FCSTD DOCUMENT  (FreeCAD 0.19R)
Label: tool_support
License: All rights reserved
LicenseURL: http://en.wikipedia.org/wiki/All_rights_reserved
objects: App::DocumentObjectGroup×2, App::Link×2, PartDesign::CoordinateSystem×1, App::FeaturePython×1, App::Part×1
note: 1 computed .brp shape members not serialized (recipe doc carries the construction recipe); baked Part::Feature solids carry a one-line shape summary decoded from their .brp
EXTERNAL_REF file=platform.FCStd obj=LCS_1
EXTERNAL_REF file=platform.FCStd obj=Body
EXTERNAL_REF file=lower_support.FCStd obj=LCS_hole1
EXTERNAL_REF file=platform.FCStd obj=LCS_hole1
EXTERNAL_REF file=lower_support.FCStd obj=Body

FEATURE [App::DocumentObjectGroup] Parts
FEATURE [PartDesign::CoordinateSystem] LCS_Origin
  AttacherType = Attacher::AttachEngine3D
  MapMode = 2
  Support = -> [X_Axis]
FEATURE [App::DocumentObjectGroup] Constraints
FEATURE [App::FeaturePython] Variables  # WARN: FeaturePython — macro-defined, semantics opaque (R4)
FEATURE [App::Link] Unnamed1_platform
  AssemblyType = Asm4EE
  AttachedBy = #LCS_1
  AttachedTo = Parent Assembly#LCS_Origin
  LinkPlacement = pos=(3e-16,-8e-16,-10) rot=(0,0,1;0rad)
  LinkedObject = -> <external platform.FCStd>#Body
  Placement = pos=(3e-16,-8e-16,-10) rot=(0,0,1;0rad)
  expr: Placement = LCS_Origin.Placement * AttachmentOffset * platform#LCS_1.Placement ^ -1
FEATURE [App::Link] lower_support_Body
  AssemblyType = Asm4EE
  AttachedBy = #LCS_hole1
  AttachedTo = Unnamed1_platform#LCS_hole1
  AttachmentOffset = pos=(0,0,0) rot=(1,0,0;3.14159rad)
  LinkPlacement = pos=(1.95e-14,100,2.03e-14) rot=(0,0,1;0rad)
  LinkedObject = -> <external lower_support.FCStd>#Body
  Placement = pos=(1.95e-14,100,2.03e-14) rot=(0,0,1;0rad)
  expr: Placement = Unnamed1_platform.Placement * platform#LCS_hole1.Placement * AttachmentOffset * lower_support#LCS_hole1.Placement ^ -1
FEATURE [App::Part] Model
  Configuration = 0
  Group = -> [LCS_Origin,Constraints,Variables,Unnamed1_platform,lower_support_Body]
  Origin = -> Origin
  Type = Assembly4 Model

RESOLVED EXTERNAL PARTS (link-assembly join: the EXTERNAL_REF files above that resolve inside this repo's crawl, each included once):
---- part lower_support.FCStd = doc fcstd_1ed02091a3f0 ----
FCSTD DOCUMENT  (FreeCAD 0.19R)
Label: lower_support
License: All rights reserved
LicenseURL: http://en.wikipedia.org/wiki/All_rights_reserved
objects: Sketcher::SketchObject×5, PartDesign::CoordinateSystem×5, PartDesign::Pad×3, PartDesign::Point×3, PartDesign::Hole×2, PartDesign::Plane×1, PartDesign::Body×1
note: 25 computed .brp shape members not serialized (recipe doc carries the construction recipe); baked Part::Feature solids carry a one-line shape summary decoded from their .brp

FEATURE [Sketcher::SketchObject] Sketch
  FullyConstrained = true
  MapMode = 5
  Placement = pos=(0,0,0) rot=(1,0,0;1.5708rad)
  Support = -> [XZ_Plane]
  sketch-geometry (8):
    g0: LineSegment StartX=-32 StartY=32 StartZ=0 EndX=32 EndY=32 EndZ=0
    g1: LineSegment StartX=-28 StartY=28 StartZ=0 EndX=-4 EndY=28 EndZ=0
    g2: LineSegment StartX=-4 StartY=4 StartZ=0 EndX=-4 EndY=28 EndZ=0
    g3: LineSegment StartX=4 StartY=28 StartZ=0 EndX=4 EndY=4 EndZ=0
    g4: LineSegment StartX=4 StartY=28 StartZ=0 EndX=28 EndY=28 EndZ=0
    g5: ArcOfCircle CenterX=-28 CenterY=32 CenterZ=0 NormalX=0 NormalY=0 NormalZ=1 AngleXU=0 Radius=4 StartAngle=3.14159 EndAngle=4.71239
    g6: ArcOfCircle CenterX=28 CenterY=32 CenterZ=0 NormalX=0 NormalY=0 NormalZ=1 AngleXU=0 Radius=4 StartAngle=4.71239 EndAngle=6.28319
    g7: ArcOfCircle CenterX=1e-16 CenterY=4 CenterZ=0 NormalX=0 NormalY=0 NormalZ=1 AngleXU=0 Radius=4 StartAngle=3.14159 EndAngle=6.28319
  constraints (25):
    c: Horizontal(g1)
    c: Coincident(g2,g1)
    c: Vertical(g2)
    c: Vertical(g3)
    c: Coincident(g4,g3)
    c: Horizontal(g4)
    c: DistanceX(g2,g3) = 8
    c: DistanceY(g4,g0) = 4
    c: DistanceX(g0,g0) = 64
    c: Symmetric(g1,g3,g-2)
    c: DistanceY(g3,g3) = 24
    c: DistanceY(g2,g1) = 24
    c: DistanceX(g3,g4) = 24
    c: DistanceX(g1,g1) = 24
    c: DistanceY(g-1,g2) = 4
    c: Symmetric(g0,g0,g-2)
    c: Coincident(g5,g0)
    c: PointOnObject(g5,g0)
    c: Coincident(g5,g1)
    c: PointOnObject(g6,g0)
    c: Coincident(g6,g4)
    c: Coincident(g6,g0)
    c: Coincident(g7,g3)
    c: Coincident(g7,g2)
    c: PointOnObject(g-1,g7)
FEATURE [PartDesign::Pad] Pad
  Direction = (1,1,1)
  Length = 200
  Length2 = 100
  Placement = pos=(0,0,0) rot=(1,0,0;1.5708rad)
  Profile = -> Sketch
  Type = 0
FEATURE [PartDesign::CoordinateSystem] LCS_1
  AttacherType = Attacher::AttachEngine3D
  MapMode = 45
  Placement = pos=(0,-200,32) rot=(0.57735,0.57735,0.57735;2.0944rad)
  Support = -> [Pad]
FEATURE [PartDesign::CoordinateSystem] LCS_2
  AttacherType = Attacher::AttachEngine3D
  MapMode = 45
  Placement = pos=(0,0,32) rot=(0.57735,0.57735,0.57735;2.0944rad)
  Support = -> [Pad]
FEATURE [PartDesign::Plane] DatumPlane
  AttachmentOffset = pos=(0,0,0) rot=(0,1,0;1.5708rad)
  Length = 288.534
  MapMode = 5
  Placement = pos=(0,0,0) rot=(-0.57735,0.57735,-0.57735;2.0944rad)
  ResizeMode = 0
  Support = -> [Pad]
  Width = 81.5341
FEATURE [Sketcher::SketchObject] Sketch001
  ExternalGeometry = -> [Pad]
  FullyConstrained = true
  MapMode = 5
  Placement = pos=(0,0,0) rot=(0.57735,-0.57735,0.57735;4.18879rad)
  Support = -> [DatumPlane]
  sketch-geometry (6):
    g0: LineSegment StartX=200 StartY=0 StartZ=0 EndX=232 EndY=-1e-15 EndZ=0
    g1: LineSegment StartX=200 StartY=0 StartZ=0 EndX=200 EndY=-32 EndZ=0
    g2: LineSegment StartX=228 StartY=-4 StartZ=0 EndX=204 EndY=-4 EndZ=0
    g3: LineSegment StartX=204 StartY=-4 StartZ=0 EndX=204 EndY=-28 EndZ=0
    g4: ArcOfCircle CenterX=228 CenterY=0 CenterZ=0 NormalX=0 NormalY=0 NormalZ=1 AngleXU=0 Radius=4 StartAngle=4.71239 EndAngle=6.28319
    g5: ArcOfCircle CenterX=200 CenterY=-28 CenterZ=0 NormalX=0 NormalY=0 NormalZ=1 AngleXU=0 Radius=4 StartAngle=4.71239 EndAngle=6.28319
  constraints (19):
    c: Coincident(g0,g-3)
    c: PointOnObject(g0,g-1)
    c: Coincident(g1,g0)
    c: Vertical(g1)
    c: Horizontal(g2)
    c: Coincident(g3,g2)
    c: Vertical(g3)
    c: DistanceX(g1,g3) = 4
    c: DistanceY(g2,g0) = 4
    c: DistanceX(g0,g0) = 32
    c: DistanceX(g2,g2) = 24
    c: DistanceY(g1,g0) = 32
    c: DistanceY(g3,g2) = 24
    c: PointOnObject(g4,g0)
    c: Coincident(g4,g2)
    c: Coincident(g4,g0)
    c: PointOnObject(g5,g1)
    c: Coincident(g5,g1)
    c: Coincident(g5,g3)
FEATURE [PartDesign::Pad] Pad001
  BaseFeature = -> Pad
  Direction = (1,1,1)
  Length = 20
  Length2 = 100
  Midplane = true
  Placement = pos=(0,0,0) rot=(1,0,0;1.5708rad)
  Profile = -> Sketch001
  Type = 0
FEATURE [Sketcher::SketchObject] Sketch002
  ExternalGeometry = -> [Pad001]
  FullyConstrained = true
  MapMode = 5
  Placement = pos=(0,0,0) rot=(0.57735,-0.57735,0.57735;4.18879rad)
  Support = -> [DatumPlane]
  expr: Constraints[9] = 32
  sketch-geometry (6):
    g0: LineSegment StartX=0 StartY=0 StartZ=0 EndX=-32 EndY=5e-16 EndZ=0
    g1: LineSegment StartX=0 StartY=0 StartZ=0 EndX=0 EndY=-32 EndZ=0
    g2: LineSegment StartX=-28 StartY=-4 StartZ=0 EndX=-4 EndY=-4 EndZ=0
    g3: LineSegment StartX=-4 StartY=-4 StartZ=0 EndX=-4 EndY=-28 EndZ=0
    g4: ArcOfCircle CenterX=-28 CenterY=0 CenterZ=0 NormalX=0 NormalY=0 NormalZ=1 AngleXU=0 Radius=4 StartAngle=3.14159 EndAngle=4.71239
    g5: ArcOfCircle CenterX=0 CenterY=-28 CenterZ=0 NormalX=0 NormalY=0 NormalZ=1 AngleXU=0 Radius=4 StartAngle=3.14159 EndAngle=4.71239
  constraints (19):
    c: Coincident(g0,g-1)
    c: PointOnObject(g0,g-1)
    c: Coincident(g1,g0)
    c: PointOnObject(g1,g-2)
    c: Horizontal(g2)
    c: Coincident(g3,g2)
    c: Vertical(g3)
    c: DistanceY(g3,g2) = 24
    c: DistanceX(g2,g2) = 24
    c: DistanceY(g1,g0) = 32
    c: DistanceX(g0,g0) = 32
    c: DistanceX(g3,g1) = 4
    c: DistanceY(g2,g0) = 4
    c: PointOnObject(g4,g0)
    c: Coincident(g4,g2)
    c: Coincident(g4,g0)
    c: PointOnObject(g5,g1)
    c: Coincident(g5,g1)
    c: Coincident(g5,g3)
FEATURE [PartDesign::Pad] Pad002
  BaseFeature = -> Pad001
  Direction = (1,1,1)
  Length = 100
  Length2 = 100
  Midplane = true
  Placement = pos=(0,0,0) rot=(1,0,0;1.5708rad)
  Profile = -> Sketch002
  Type = 0
FEATURE [Sketcher::SketchObject] Sketch003
  ExternalGeometry = -> [Pad002]
  FullyConstrained = true
  MapMode = 5
  Placement = pos=(0,0,-6.4e-15) rot=(1,0,0;3.14159rad)
  Support = -> [Pad002]
  sketch-geometry (1):
    g0: Circle CenterX=0 CenterY=216 CenterZ=0 NormalX=0 NormalY=0 NormalZ=1 AngleXU=0 Radius=3.25
  constraints (3):
    c: DistanceY(g0,g-3) = 16
    c: PointOnObject(g0,g-2)
    c: Diameter(g0) = 6.5
FEATURE [PartDesign::Hole] Hole
  BaseFeature = -> Pad002
  Depth = 25
  DepthType = 0
  Diameter = 6
  DrillForDepth = false
  DrillPoint = 1
  DrillPointAngle = 118
  HoleCutCountersinkAngle = 90
  HoleCutCustomValues = false
  HoleCutDepth = 0
  HoleCutDiameter = 6.1
  HoleCutType = 0
  ModelActualThread = false
  Placement = pos=(0,0,0) rot=(1,0,0;1.5708rad)
  Profile = -> Sketch003
  Tapered = false
  TaperedAngle = 90
  ThreadAngle = 0
  ThreadClass = 0
  ThreadCutOffInner = 0
  ThreadCutOffOuter = 0
  ThreadDirection = 0
  ThreadFit = 0
  ThreadPitch = 0
  ThreadSize = 0
  ThreadType = 0
  Threaded = false
FEATURE [Sketcher::SketchObject] Sketch004
  ExternalGeometry = -> [Hole]
  FullyConstrained = true
  MapMode = 5
  Placement = pos=(0,0,0) rot=(1,0,0;3.14159rad)
  Support = -> [Hole]
  sketch-geometry (2):
    g0: Circle CenterX=34 CenterY=-16 CenterZ=0 NormalX=0 NormalY=0 NormalZ=1 AngleXU=0 Radius=3.25
    g1: Circle CenterX=-34 CenterY=-16 CenterZ=0 NormalX=0 NormalY=0 NormalZ=1 AngleXU=0 Radius=3.25
  constraints (5):
    c: Equal(g0,g1)
    c: Diameter(g1) = 6.5
    c: Symmetric(g1,g0,g-2)
    c: DistanceX(g-4,g1) = 16
    c: DistanceY(g-4,g1) = 16
FEATURE [PartDesign::Hole] Hole001
  BaseFeature = -> Hole
  Depth = 25
  DepthType = 0
  Diameter = 6
  DrillForDepth = false
  DrillPoint = 1
  DrillPointAngle = 118
  HoleCutCountersinkAngle = 90
  HoleCutCustomValues = false
  HoleCutDepth = 0
  HoleCutDiameter = 6.1
  HoleCutType = 0
  ModelActualThread = false
  Placement = pos=(0,0,0) rot=(1,0,0;1.5708rad)
  Profile = -> Sketch004
  Tapered = false
  TaperedAngle = 90
  ThreadAngle = 0
  ThreadClass = 0
  ThreadCutOffInner = 0
  ThreadCutOffOuter = 0
  ThreadDirection = 0
  ThreadFit = 0
  ThreadPitch = 0
  ThreadSize = 0
  ThreadType = 0
  Threaded = false
FEATURE [PartDesign::CoordinateSystem] LCS_hole2
  AttacherType = Attacher::AttachEngine3D
  MapMode = 11
  Placement = pos=(34,16,-2.9e-14) rot=(0.707107,0.707107,0;3.14159rad)
  Support = -> [Hole001]
FEATURE [PartDesign::CoordinateSystem] LCS_hole3
  AttacherType = Attacher::AttachEngine3D
  MapMode = 11
  Placement = pos=(-34,16,-2.9e-14) rot=(0.707107,0.707107,0;3.14159rad)
  Support = -> [Hole001]
FEATURE [PartDesign::CoordinateSystem] LCS_hole1
  AttacherType = Attacher::AttachEngine3D
  MapMode = 11
  Placement = pos=(0,-216,3.84e-13) rot=(0.707107,0.707107,0;3.14159rad)
  Support = -> [Hole001]
FEATURE [PartDesign::Point] DatumPoint
  AttacherType = Attacher::AttachEnginePoint
  MapMode = 36
  Placement = pos=(34,16,-2.9e-14) rot=(0,-0.707107,0.707107;3.14159rad)
  Support = -> [Hole001]
FEATURE [PartDesign::Point] DatumPoint001
  AttacherType = Attacher::AttachEnginePoint
  MapMode = 36
  Placement = pos=(-34,16,-2.9e-14) rot=(0,-0.707107,0.707107;3.14159rad)
  Support = -> [Hole001]
FEATURE [PartDesign::Point] DatumPoint002
  AttacherType = Attacher::AttachEnginePoint
  MapMode = 36
  Placement = pos=(0,-216,3.84e-13) rot=(0,-0.707107,0.707107;3.14159rad)
  Support = -> [Hole001]
FEATURE [PartDesign::Body] Body
  Group = -> [Sketch,Pad,LCS_1,LCS_2,DatumPlane,Sketch001,Pad001,Sketch002,Pad002,Sketch003,Hole,Sketch004,Hole001,LCS_hole2,LCS_hole3,LCS_hole1,DatumPoint,DatumPoint001,DatumPoint002]
  Origin = -> Origin
  Tip = -> Hole001
---- part platform.FCStd = doc fcstd_8a13aa23e370 ----
FCSTD DOCUMENT  (FreeCAD 0.19R)
Label: platform
License: All rights reserved
LicenseURL: http://en.wikipedia.org/wiki/All_rights_reserved
objects: Sketcher::SketchObject×2, PartDesign::CoordinateSystem×2, PartDesign::Pad×1, PartDesign::Hole×1, PartDesign::Body×1
note: 9 computed .brp shape members not serialized (recipe doc carries the construction recipe); baked Part::Feature solids carry a one-line shape summary decoded from their .brp

FEATURE [Sketcher::SketchObject] Sketch
  FullyConstrained = true
  MapMode = 5
  Support = -> [XY_Plane]
  sketch-geometry (4):
    g0: LineSegment StartX=-75 StartY=136 StartZ=0 EndX=75 EndY=136 EndZ=0
    g1: LineSegment StartX=75 StartY=136 StartZ=0 EndX=75 EndY=-136 EndZ=0
    g2: LineSegment StartX=75 StartY=-136 StartZ=0 EndX=-75 EndY=-136 EndZ=0
    g3: LineSegment StartX=-75 StartY=-136 StartZ=0 EndX=-75 EndY=136 EndZ=0
  constraints (10):
    c: Coincident(g0,g1)
    c: Coincident(g1,g2)
    c: Coincident(g2,g3)
    c: Coincident(g3,g0)
    c: Horizontal(g2)
    c: Vertical(g1)
    c: Symmetric(g0,g0,g-2)
    c: Symmetric(g2,g0,g-1)
    c: DistanceX(g0,g0) = 150
    c: DistanceY(g2,g0) = 272
FEATURE [PartDesign::Pad] Pad
  Direction = (1,1,1)
  Length = 10
  Length2 = 100
  Profile = -> Sketch
  Type = 0
FEATURE [PartDesign::CoordinateSystem] LCS_1
  AttacherType = Attacher::AttachEngine3D
  MapMode = 45
  Placement = pos=(-3e-16,8e-16,10) rot=(0,0,1;0rad)
  Support = -> [Pad]
FEATURE [Sketcher::SketchObject] Sketch001
  ExternalGeometry = -> [Pad]
  FullyConstrained = true
  MapMode = 5
  Placement = pos=(0,0,10) rot=(0,0,1;0rad)
  Support = -> [Pad]
  sketch-geometry (3):
    g0: Circle CenterX=0 CenterY=-116 CenterZ=0 NormalX=0 NormalY=0 NormalZ=1 AngleXU=0 Radius=3.25
    g1: Circle CenterX=-34 CenterY=116 CenterZ=0 NormalX=0 NormalY=0 NormalZ=1 AngleXU=0 Radius=3.25
    g2: Circle CenterX=34 CenterY=116 CenterZ=0 NormalX=0 NormalY=0 NormalZ=1 AngleXU=0 Radius=3.25
  constraints (8):
    c: PointOnObject(g0,g-2)
    c: Diameter(g0) = 6.5
    c: DistanceY(g-3,g0) = 20
    c: Symmetric(g1,g2,g-2)
    c: DistanceX(g1,g2) = 68
    c: DistanceY(g0,g2) = 232
    c: Equal(g1,g0)
    c: Equal(g0,g2)
FEATURE [PartDesign::Hole] Hole
  BaseFeature = -> Pad
  Depth = 25
  DepthType = 0
  Diameter = 6
  DrillForDepth = false
  DrillPoint = 1
  DrillPointAngle = 118
  HoleCutCountersinkAngle = 90
  HoleCutCustomValues = false
  HoleCutDepth = 0
  HoleCutDiameter = 6.1
  HoleCutType = 0
  ModelActualThread = false
  Profile = -> Sketch001
  Tapered = false
  TaperedAngle = 90
  ThreadAngle = 0
  ThreadClass = 0
  ThreadCutOffInner = 0
  ThreadCutOffOuter = 0
  ThreadDirection = 0
  ThreadFit = 0
  ThreadPitch = 0
  ThreadSize = 0
  ThreadType = 0
  Threaded = false
FEATURE [PartDesign::CoordinateSystem] LCS_hole1
  AttacherType = Attacher::AttachEngine3D
  MapMode = 11
  Placement = pos=(0,-116,10) rot=(0,0,1;1.5708rad)
  Support = -> [Hole]
FEATURE [PartDesign::Body] Body  label="platform"
  Group = -> [Sketch,Pad,LCS_1,Sketch001,Hole,LCS_hole1]
  Origin = -> Origin
  Tip = -> Hole
